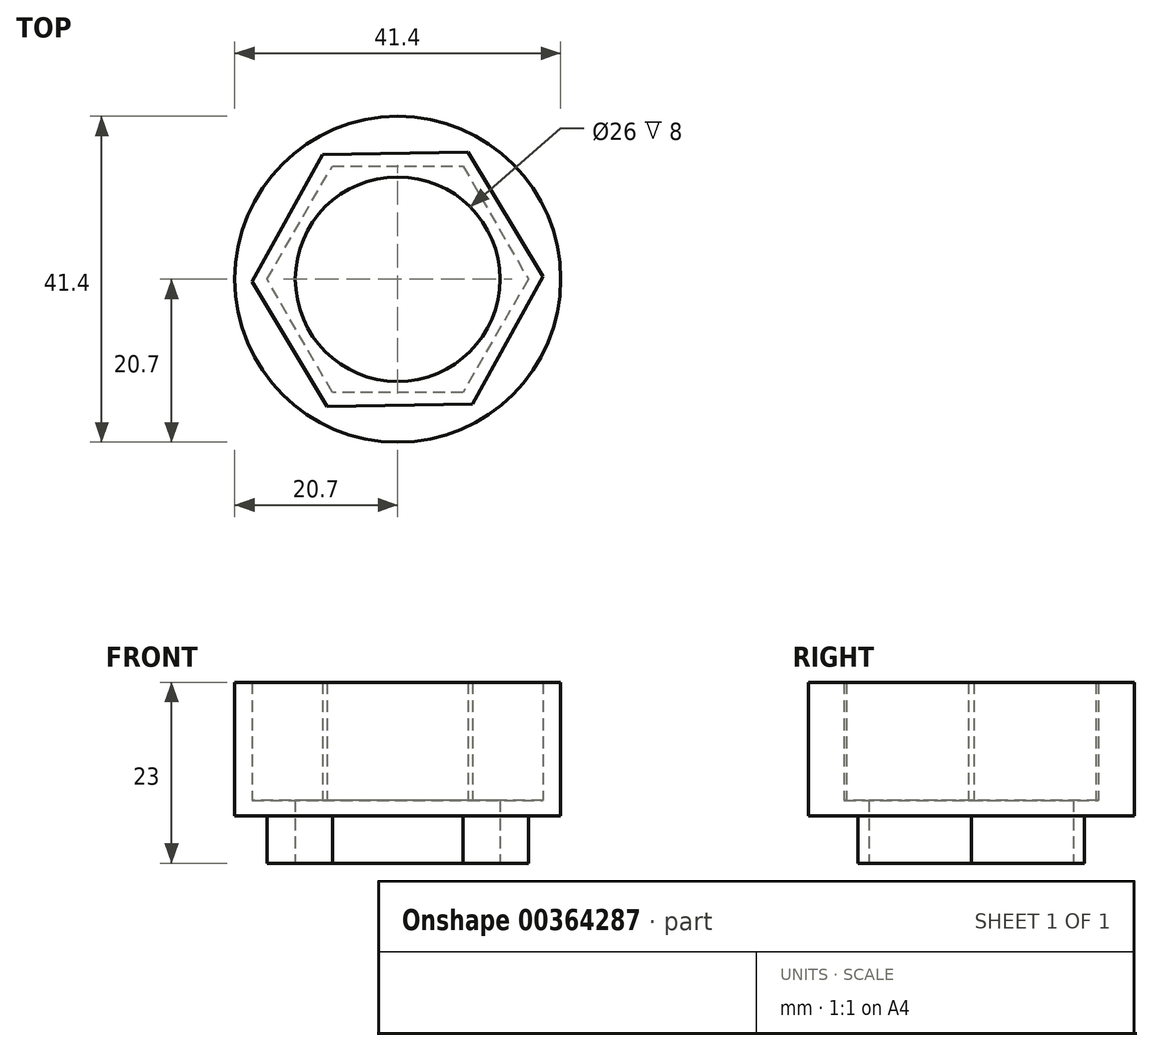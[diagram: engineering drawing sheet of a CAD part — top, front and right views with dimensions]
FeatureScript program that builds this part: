
annotation { "Feature Type Name" : "Feature", "Feature Type Description" : "" }
export const myFeature = defineFeature(function(context is Context, id is Id, definition is map)
    precondition{}
    {
        {
            var Q0;
            Q0=qCreatedBy(makeId("Top.planeOp"),FACE);
            var sketch = newSketch(context, id + "F0", { "sketchPlane" : qUnion([Q0])});
            skCircle(sketch, "E0.cCircle", {"center": v(0, 0) * mm, "radius": 14.38 * mm, "construction": true});
            skLineSegment(sketch, "E0.0", {"start": v(-8.3, 14.38) * mm, "end": v(8.3, 14.38) * mm});
            skLineSegment(sketch, "E0.1", {"start": v(8.3, 14.38) * mm, "end": v(16.6, 0) * mm});
            skLineSegment(sketch, "E0.2", {"start": v(16.6, 0) * mm, "end": v(8.3, -14.37) * mm});
            skLineSegment(sketch, "E0.3", {"start": v(8.3, -14.37) * mm, "end": v(-8.3, -14.38) * mm});
            skLineSegment(sketch, "E0.4", {"start": v(-8.3, -14.38) * mm, "end": v(-16.6, 0) * mm});
            skLineSegment(sketch, "E0.5", {"start": v(-16.6, 0) * mm, "end": v(-8.3, 14.37) * mm});
            skPoint(sketch, "E0.0.midPoint", {"position": v(0, 14.38) * mm});
            skSolve(sketch);
        }
        {
            var Q0;
            Q0 = qSketchRegion(id + "F0", true);
            extrude(context, id + "F1", {"entities" : qUnion([Q0]), "depth" : 6 * mm});
        }
        {
            var Q0;
            Q0=makeQuery(id+"F1.opExtrude","CAP_FACE",FACE,{"disambiguationData":[OSD([sQuery(id+"F0.wireOp",EDGE,"E0.0"),sQuery(id+"F0.wireOp",EDGE,"E0.1"),sQuery(id+"F0.wireOp",EDGE,"E0.2"),sQuery(id+"F0.wireOp",EDGE,"E0.3"),sQuery(id+"F0.wireOp",EDGE,"E0.4"),sQuery(id+"F0.wireOp",EDGE,"E0.5")])],"isStart":false});
            var sketch = newSketch(context, id + "F2", { "sketchPlane" : qUnion([Q0])});
            skCircle(sketch, "E1", {"center": v(0, 0) * mm, "radius": 20.7 * mm});
            skSolve(sketch);
        }
        {
            var Q0;
            Q0 = qSketchRegion(id + "F2", true);
            extrude(context, id + "F3", {"entities" : qUnion([Q0]), "operationType" : NewBodyOperationType.ADD, "depth" : 2 * mm});
        }
        {
            var Q0;
            Q0=makeQuery(id+"F3.opExtrude","CAP_FACE",FACE,{"disambiguationData":[OSD([sQuery(id+"F2.wireOp",EDGE,"E1")])],"isStart":false});
            var sketch = newSketch(context, id + "F4", { "sketchPlane" : qUnion([Q0])});
            skCircle(sketch, "E2.cCircle", {"center": v(0, 0) * mm, "radius": 16 * mm, "construction": true});
            skLineSegment(sketch, "E2.0", {"start": v(8.95, 16.16) * mm, "end": v(18.47, 0.33) * mm});
            skLineSegment(sketch, "E2.1", {"start": v(18.47, 0.33) * mm, "end": v(9.52, -15.83) * mm});
            skLineSegment(sketch, "E2.2", {"start": v(9.52, -15.83) * mm, "end": v(-8.95, -16.16) * mm});
            skLineSegment(sketch, "E2.3", {"start": v(-8.95, -16.16) * mm, "end": v(-18.47, -0.33) * mm});
            skLineSegment(sketch, "E2.4", {"start": v(-18.47, -0.33) * mm, "end": v(-9.52, 15.83) * mm});
            skLineSegment(sketch, "E2.5", {"start": v(-9.52, 15.83) * mm, "end": v(8.95, 16.16) * mm});
            skPoint(sketch, "E2.0.midPoint", {"position": v(13.71, 8.25) * mm});
            skCircle(sketch, "E3.0", {"center": v(0, 0) * mm, "radius": 20.7 * mm});
            skSolve(sketch);
        }
        {
            var Q0;
            Q0 = qSketchRegion(id + "F4", true);
            extrude(context, id + "F5", {"entities" : qUnion([Q0]), "operationType" : NewBodyOperationType.ADD, "depth" : 15 * mm});
        }
        {
            var Q0;
            Q0=makeQuery(id+"F1.opExtrude","CAP_FACE",FACE,{"disambiguationData":[OSD([sQuery(id+"F0.wireOp",EDGE,"E0.0"),sQuery(id+"F0.wireOp",EDGE,"E0.1"),sQuery(id+"F0.wireOp",EDGE,"E0.2"),sQuery(id+"F0.wireOp",EDGE,"E0.3"),sQuery(id+"F0.wireOp",EDGE,"E0.4"),sQuery(id+"F0.wireOp",EDGE,"E0.5")])],"isStart":true});
            var sketch = newSketch(context, id + "F6", { "sketchPlane" : qUnion([Q0])});
            skCircle(sketch, "E4", {"center": v(0, 0) * mm, "radius": 13 * mm});
            skSolve(sketch);
        }
        {
            var Q0;
            Q0 = qSketchRegion(id + "F6", true);
            extrude(context, id + "F7", {"entities" : qUnion([Q0]), "operationType" : NewBodyOperationType.REMOVE, "oppositeDirection" : true, "depth" : 25 * mm});
        }
    });
